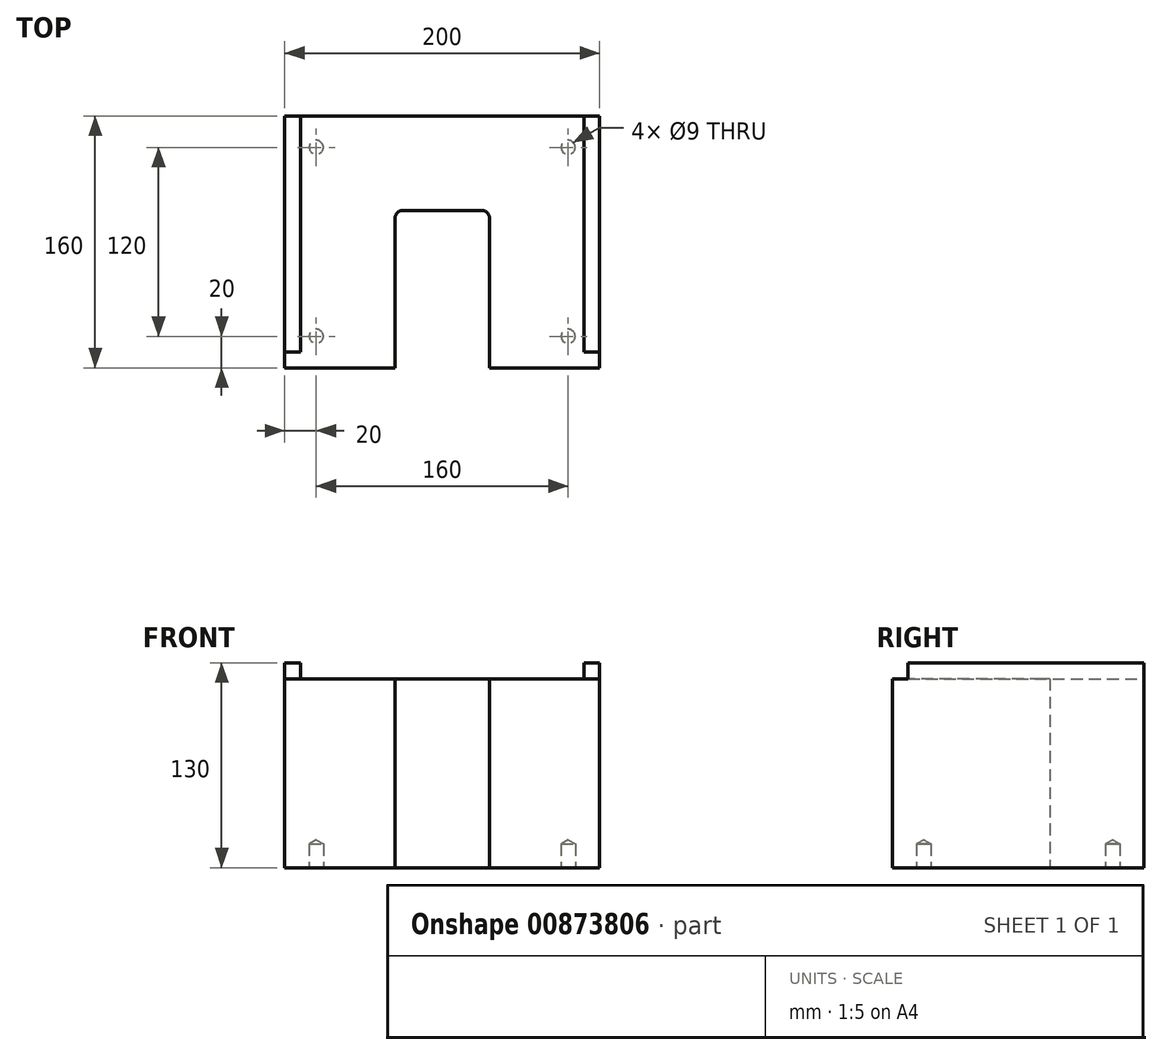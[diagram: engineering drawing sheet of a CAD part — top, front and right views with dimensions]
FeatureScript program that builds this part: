
annotation { "Feature Type Name" : "Feature", "Feature Type Description" : "" }
export const myFeature = defineFeature(function(context is Context, id is Id, definition is map)
    precondition{}
    {
        {
            var Q0;
            Q0=qCreatedBy(makeId("Top.planeOp"),FACE);
            var sketch = newSketch(context, id + "F0", { "sketchPlane" : qUnion([Q0])});
            skLineSegment(sketch, "E0.bottom", {"start": v(100, 80) * mm, "end": v(-100, 80) * mm});
            skLineSegment(sketch, "E0.top", {"start": v(100, -80) * mm, "end": v(55, -80) * mm});
            skLineSegment(sketch, "E0.left", {"start": v(100, 80) * mm, "end": v(100, -80) * mm});
            skLineSegment(sketch, "E0.right", {"start": v(-100, 80) * mm, "end": v(-100, -80) * mm});
            skLineSegment(sketch, "E1.trimOffspring", {"start": v(-55, -80) * mm, "end": v(-100, -80) * mm});
            skLineSegment(sketch, "E2", {"start": v(-55, -80) * mm, "end": v(55, -80) * mm});
            skLineSegment(sketch, "E3", {"start": v(0, -10) * mm, "end": v(0, -128.54) * mm});
            skPoint(sketch, "E3.endSnap0", {"position": v(0, -80) * mm});
            skLineSegment(sketch, "E4.0.left", {"start": v(30, -80) * mm, "end": v(30, -88.75) * mm});
            skLineSegment(sketch, "E4.0.right", {"start": v(-30, -10) * mm, "end": v(-30, -80) * mm});
            skLineSegment(sketch, "E5.top", {"start": v(0, -88.75) * mm, "end": v(-30, -88.75) * mm});
            skLineSegment(sketch, "E5.left", {"start": v(30, -16.37) * mm, "end": v(30, -88.75) * mm});
            skPoint(sketch, "E5.middle", {"position": v(0, -10) * mm});
            skPoint(sketch, "E6.orphan", {"position": v(30, 68.75) * mm});
            skPoint(sketch, "E7.orphan", {"position": v(-30, 68.75) * mm});
            skLineSegment(sketch, "E8.bottom", {"start": v(30, 20) * mm, "end": v(-30, 20) * mm});
            skLineSegment(sketch, "E8.top", {"start": v(30, -180) * mm, "end": v(-30, -180) * mm});
            skLineSegment(sketch, "E8.left", {"start": v(30, 20) * mm, "end": v(30, -180) * mm});
            skLineSegment(sketch, "E8.right", {"start": v(-30, 20) * mm, "end": v(-30, -180) * mm});
            skSolve(sketch);
        }
        {
            var Q0;
            Q0=makeQuery(id+"F0.imprint","IMPRINT",FACE,{"disambiguationData":[TD([[makeQuery(id+"F0.imprint","IMPRINT",EDGE,{"derivedFrom":sQuery(id+"F0.wireOp",EDGE,"E0.bottom")}),1.0]])]});
            extrude(context, id + "F1", {"entities" : qUnion([Q0]), "depth" : 120 * mm, "offsetDistance" : 25 * mm});
        }
        {
            var Q0;
            Q0=makeQuery(id+"F1.opExtrude","CAP_FACE",FACE,{"disambiguationData":[OSD([sQuery(id+"F0.wireOp",EDGE,"E0.bottom"),sQuery(id+"F0.wireOp",EDGE,"E0.top"),sQuery(id+"F0.wireOp",EDGE,"E0.left"),sQuery(id+"F0.wireOp",EDGE,"E0.right"),sQuery(id+"F0.wireOp",EDGE,"E1.trimOffspring"),sQuery(id+"F0.wireOp",EDGE,"E2"),sQuery(id+"F0.wireOp",EDGE,"E4.0.startCap"),sQuery(id+"F0.wireOp",EDGE,"E4.0.left"),sQuery(id+"F0.wireOp",EDGE,"E4.0.right")])],"isStart":true});
            var sketch = newSketch(context, id + "F2", { "sketchPlane" : qUnion([Q0])});
            skLineSegment(sketch, "E9.bottom", {"start": v(80, -60) * mm, "end": v(-80, -60) * mm, "construction": true});
            skLineSegment(sketch, "E9.top", {"start": v(80, 60) * mm, "end": v(-80, 60) * mm, "construction": true});
            skLineSegment(sketch, "E9.left", {"start": v(80, -60) * mm, "end": v(80, 60) * mm, "construction": true});
            skLineSegment(sketch, "E9.right", {"start": v(-80, -60) * mm, "end": v(-80, 60) * mm, "construction": true});
            skPoint(sketch, "E9.middle", {"position": v(0, 0) * mm});
            skCircle(sketch, "E10", {"center": v(80, 60) * mm, "radius": 5 * mm});
            skCircle(sketch, "E11", {"center": v(80, -60) * mm, "radius": 5 * mm});
            skCircle(sketch, "E12", {"center": v(-80, -60) * mm, "radius": 5 * mm});
            skCircle(sketch, "E13", {"center": v(-80, 60) * mm, "radius": 5 * mm});
            skSolve(sketch);
        }
        {
            var Q0;
            Q0=makeQuery(id+"F1.opExtrude","CAP_FACE",FACE,{"disambiguationData":[OSD([sQuery(id+"F0.wireOp",EDGE,"E0.bottom"),sQuery(id+"F0.wireOp",EDGE,"E0.top"),sQuery(id+"F0.wireOp",EDGE,"E0.left"),sQuery(id+"F0.wireOp",EDGE,"E0.right"),sQuery(id+"F0.wireOp",EDGE,"pt1L4xHU-Gnce-Inzv-dWWJ-iYGtCXfDHGIm.top"),sQuery(id+"F0.wireOp",EDGE,"pt1L4xHU-Gnce-Inzv-dWWJ-iYGtCXfDHGIm.left"),sQuery(id+"F0.wireOp",EDGE,"pt1L4xHU-Gnce-Inzv-dWWJ-iYGtCXfDHGIm.right"),sQuery(id+"F0.wireOp",EDGE,"KFp5Eu1j-urzi-dJdu-wyPm-XwG6DOZos1A6"),sQuery(id+"F0.wireOp",EDGE,"azy8M7ay-xqtP-hNJj-Wd54-KBBLuS1Ml3In"),sQuery(id+"F0.wireOp",EDGE,"E1.trimOffspring")])],"isStart":false});
            var sketch = newSketch(context, id + "F3", { "sketchPlane" : qUnion([Q0])});
            skLineSegment(sketch, "E14.bottom", {"start": v(-100, -80) * mm, "end": v(-80, -80) * mm});
            skLineSegment(sketch, "E14.top", {"start": v(-100, -60) * mm, "end": v(-80, -60) * mm});
            skLineSegment(sketch, "E14.left", {"start": v(-100, -80) * mm, "end": v(-100, -60) * mm});
            skLineSegment(sketch, "E14.right", {"start": v(-80, -80) * mm, "end": v(-80, -60) * mm});
            skLineSegment(sketch, "E15.bottom", {"start": v(-100, 80) * mm, "end": v(-80, 80) * mm});
            skLineSegment(sketch, "E15.top", {"start": v(-100, 60) * mm, "end": v(-80, 60) * mm});
            skLineSegment(sketch, "E15.left", {"start": v(-100, 80) * mm, "end": v(-100, 60) * mm});
            skLineSegment(sketch, "E15.right", {"start": v(-80, 80) * mm, "end": v(-80, 60) * mm});
            skLineSegment(sketch, "E16.bottom", {"start": v(100, 80) * mm, "end": v(80, 80) * mm});
            skLineSegment(sketch, "E16.top", {"start": v(100, 60) * mm, "end": v(80, 60) * mm});
            skLineSegment(sketch, "E16.left", {"start": v(100, 80) * mm, "end": v(100, 60) * mm});
            skLineSegment(sketch, "E16.right", {"start": v(80, 80) * mm, "end": v(80, 60) * mm});
            skLineSegment(sketch, "E17.bottom", {"start": v(100, -80) * mm, "end": v(80, -80) * mm});
            skLineSegment(sketch, "E17.top", {"start": v(100, -60) * mm, "end": v(80, -60) * mm});
            skLineSegment(sketch, "E17.left", {"start": v(100, -80) * mm, "end": v(100, -60) * mm});
            skLineSegment(sketch, "E17.right", {"start": v(80, -80) * mm, "end": v(80, -60) * mm});
            skSolve(sketch);
        }
        {
            var Q0;
            Q0=makeQuery(id+"F1.opExtrude","SWEPT_FACE",FACE,{"disambiguationData":[OSD([sQuery(id+"F0.wireOp",EDGE,"E0.bottom")])]});
            var sketch = newSketch(context, id + "F4", { "sketchPlane" : qUnion([Q0])});
            skLineSegment(sketch, "E18.left", {"start": v(-100, 120) * mm, "end": v(-100, 130) * mm});
            skLineSegment(sketch, "E19.bottom", {"start": v(-100, 120) * mm, "end": v(-90, 120) * mm});
            skLineSegment(sketch, "E19.top", {"start": v(-100, 130) * mm, "end": v(-90, 130) * mm});
            skLineSegment(sketch, "E19.right", {"start": v(-90, 120) * mm, "end": v(-90, 130) * mm});
            skLineSegment(sketch, "E20.bottom", {"start": v(100, 120) * mm, "end": v(90, 120) * mm});
            skLineSegment(sketch, "E20.top", {"start": v(100, 130) * mm, "end": v(90, 130) * mm});
            skLineSegment(sketch, "E20.left", {"start": v(100, 120) * mm, "end": v(100, 130) * mm});
            skLineSegment(sketch, "E20.right", {"start": v(90, 120) * mm, "end": v(90, 130) * mm});
            skSolve(sketch);
        }
        {
            var Q0;
            Q0=makeQuery(id+"F4.imprint","IMPRINT",FACE,{"disambiguationData":[TD([[makeQuery(id+"F4.imprint","IMPRINT",EDGE,{"derivedFrom":sQuery(id+"F4.wireOp",EDGE,"JXAhHfXm-zThM-Iakw-wxTa-Ka0YrSe1jMAB.bottom")}),-1.0]])]});
            var Q1;
            Q1=makeQuery(id+"F4.imprint","IMPRINT",FACE,{"disambiguationData":[TD([[makeQuery(id+"F4.imprint","IMPRINT",EDGE,{"derivedFrom":sQuery(id+"F4.wireOp",EDGE,"A8Ny9522-XGlY-eOJh-37T3-ZuelKpozTCaC.bottom")}),-1.0]])]});
            var Q2;
            Q2=makeQuery(id+"F4.imprint","IMPRINT",FACE,{"disambiguationData":[TD([[makeQuery(id+"F4.imprint","IMPRINT",EDGE,{"derivedFrom":sQuery(id+"F4.wireOp",EDGE,"E18.bottom")}),-1.0]])]});
            var Q3;
            Q3=makeQuery(id+"F4.imprint","IMPRINT",FACE,{"disambiguationData":[TD([[makeQuery(id+"F4.imprint","IMPRINT",EDGE,{"derivedFrom":sQuery(id+"F4.wireOp",EDGE,"JXAhHfXm-zThM-Iakw-wxTa-Ka0YrSe1jMAB.bottom")}),1.0]])]});
            var Q4;
            Q4=makeQuery(id+"F4.imprint","IMPRINT",FACE,{"disambiguationData":[TD([[makeQuery(id+"F4.imprint","IMPRINT",EDGE,{"derivedFrom":sQuery(id+"F4.wireOp",EDGE,"E20.bottom")}),1.0]])]});
            var Q5;
            Q5=makeQuery(id+"F4.imprint","IMPRINT",FACE,{"disambiguationData":[TD([[makeQuery(id+"F4.imprint","IMPRINT",EDGE,{"derivedFrom":sQuery(id+"F4.wireOp",EDGE,"E19.bottom")}),1.0]])]});
            extrude(context, id + "F5", {"entities" : qUnion([Q0, Q1, Q2, Q3, Q4, Q5]), "operationType" : NewBodyOperationType.ADD, "oppositeDirection" : true, "depth" : 150 * mm, "offsetDistance" : 25 * mm});
        }
        {
            var Q0;
            Q0=sQuery(id+"F2.wireOp",VERTEX,"E9.bottom.end");
            var Q1;
            Q1=sQuery(id+"F2.wireOp",VERTEX,"E9.top.end");
            var Q2;
            Q2=sQuery(id+"F2.wireOp",VERTEX,"E9.top.start");
            var Q3;
            Q3=sQuery(id+"F2.wireOp",VERTEX,"E9.bottom.start");
            var Q4;
            Q4=makeQuery(id+"F1.opExtrude","SWEPT_BODY",BODY,{"disambiguationData":[OSD([sQuery(id+"F0.wireOp",EDGE,"E0.bottom"),sQuery(id+"F0.wireOp",EDGE,"E0.top"),sQuery(id+"F0.wireOp",EDGE,"E0.left"),sQuery(id+"F0.wireOp",EDGE,"E0.right"),sQuery(id+"F0.wireOp",EDGE,"E1.trimOffspring"),sQuery(id+"F0.wireOp",EDGE,"E2"),sQuery(id+"F0.wireOp",EDGE,"E4.0.startCap"),sQuery(id+"F0.wireOp",EDGE,"E4.0.left"),sQuery(id+"F0.wireOp",EDGE,"E4.0.right")])]});
            hole(context, id + "F6", {"style" : HoleStyle.SIMPLE, "endStyle" : HoleEndStyle.BLIND, "standardTappedOrClearance" : lookupTablePath({ "fit" : "Normal", "standard" : "ISO", "size" : "M8", "type" : "Clearance" }), "standardBlindInLast" : lookupTablePath({ "fit" : "Normal", "standard" : "ISO", "engagement" : "75%", "pitch" : "1.25 mm", "size" : "M8", "type" : "Clearance & tapped" }), "holeDiameter" : 9 * mm, "majorDiameter" : 5 * mm, "holeDepth" : 15 * mm, "isTappedThrough" : true, "tappedDepth" : 12 * mm, "tapClearance" : 3, "locations" : qUnion([Q0, Q1, Q2, Q3]), "scope" : qUnion([Q4])});
        }
        {
            var Q0;
            Q0=makeQuery(id+"F1.opExtrude","SWEPT_EDGE",EDGE,{"disambiguationData":[OSD([sQuery(id+"F0.wireOp",EDGE,"E8.bottom"),sQuery(id+"F0.wireOp",EDGE,"E8.right")])]});
            var Q1;
            Q1=makeQuery(id+"F1.opExtrude","SWEPT_EDGE",EDGE,{"disambiguationData":[OSD([sQuery(id+"F0.wireOp",EDGE,"E8.bottom"),sQuery(id+"F0.wireOp",EDGE,"E8.left")])]});
            fillet(context, id + "F7", {"entities" : qUnion([Q0, Q1]), "tangentPropagation" : true, "radius" : 5 * mm, "defaultsChanged" : false, "vertexSettings" : [], "allowEdgeOverflow" : false});
        }
    });
